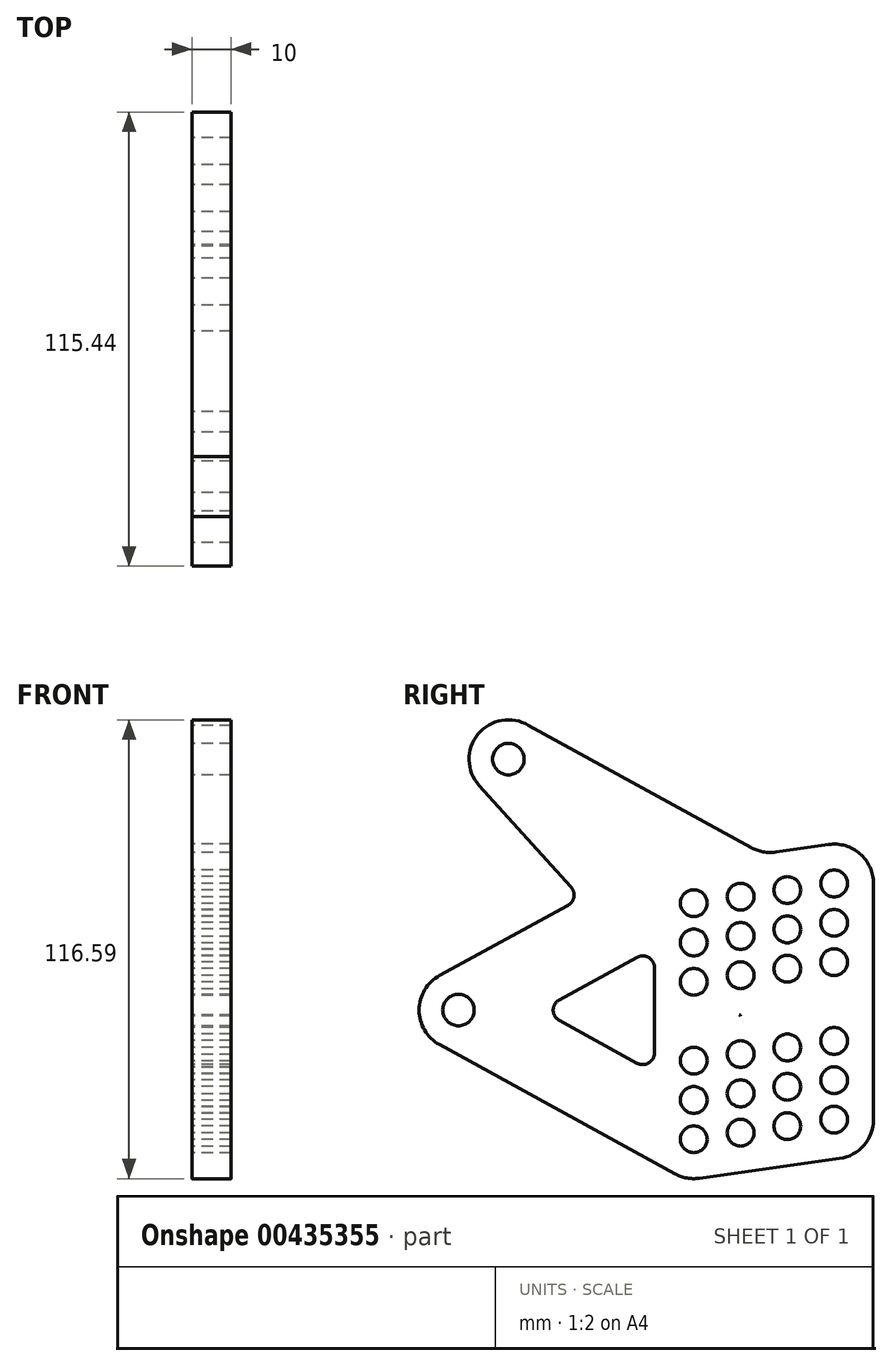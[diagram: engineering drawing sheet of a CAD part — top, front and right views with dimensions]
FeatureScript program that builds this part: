
annotation { "Feature Type Name" : "Feature", "Feature Type Description" : "" }
export const myFeature = defineFeature(function(context is Context, id is Id, definition is map)
    precondition{}
    {
        {
            var Q0;
            Q0=qCreatedBy(makeId("Right.planeOp"),FACE);
            var sketch = newSketch(context, id + "F0", { "sketchPlane" : qUnion([Q0])});
            skCircle(sketch, "E0", {"center": v(-13.5, -7.97) * mm, "radius": 4 * mm});
            skCircle(sketch, "E1", {"center": v(-0.82, 55.78) * mm, "radius": 4 * mm});
            skCircle(sketch, "E2", {"center": v(106.29, -0.8) * mm, "radius": 3.4 * mm});
            skPoint(sketch, "E3.start.orphan", {"position": v(-0.67, 56.85) * mm});
            skPoint(sketch, "E4.start.orphan", {"position": v(-13.3, -6.9) * mm});
            skLineSegment(sketch, "E5.trimOffspring", {"start": v(102.9, -1.01) * mm, "end": v(106.29, -0.8) * mm});
            skLineSegment(sketch, "E6", {"start": v(106.29, -0.8) * mm, "end": v(102.89, -0.8) * mm});
            skCircle(sketch, "E7", {"center": v(46.29, -0.8) * mm, "radius": 3.4 * mm});
            skCircle(sketch, "E8", {"center": v(46.29, -40.8) * mm, "radius": 3.4 * mm});
            skLineSegment(sketch, "E9", {"start": v(70.06, -0.8) * mm, "end": v(70.06, -4.07) * mm});
            skLineSegment(sketch, "E10", {"start": v(79.19, -26.2) * mm, "end": v(78.57, -26.28) * mm});
            skCircle(sketch, "E11", {"center": v(46.29, -30.8) * mm, "radius": 3.4 * mm});
            skCircle(sketch, "E12", {"center": v(46.29, -20.8) * mm, "radius": 3.4 * mm});
            skCircle(sketch, "E13", {"center": v(46.29, 9.2) * mm, "radius": 3.4 * mm});
            skCircle(sketch, "E14", {"center": v(46.29, 19.2) * mm, "radius": 3.4 * mm});
            skCircle(sketch, "E15", {"center": v(58.17, 20.86) * mm, "radius": 3.4 * mm});
            skCircle(sketch, "E16", {"center": v(58.17, 0.86) * mm, "radius": 3.4 * mm});
            skCircle(sketch, "E17", {"center": v(70.06, 12.53) * mm, "radius": 3.4 * mm});
            skCircle(sketch, "E18", {"center": v(58.17, 10.86) * mm, "radius": 3.4 * mm});
            skCircle(sketch, "E19", {"center": v(70.06, 2.53) * mm, "radius": 3.4 * mm});
            skCircle(sketch, "E20", {"center": v(81.94, 4.2) * mm, "radius": 3.4 * mm});
            skCircle(sketch, "E21", {"center": v(81.94, 14.2) * mm, "radius": 3.4 * mm});
            skCircle(sketch, "E22", {"center": v(81.94, 24.2) * mm, "radius": 3.4 * mm});
            skCircle(sketch, "E23", {"center": v(70.06, 22.53) * mm, "radius": 3.4 * mm});
            skCircle(sketch, "E24", {"center": v(58.17, -19.14) * mm, "radius": 3.4 * mm});
            skCircle(sketch, "E25", {"center": v(70.06, -17.47) * mm, "radius": 3.4 * mm});
            skCircle(sketch, "E26", {"center": v(81.94, -15.8) * mm, "radius": 3.4 * mm});
            skCircle(sketch, "E27", {"center": v(58.17, -29.14) * mm, "radius": 3.4 * mm});
            skCircle(sketch, "E28", {"center": v(70.06, -27.47) * mm, "radius": 3.4 * mm});
            skCircle(sketch, "E29", {"center": v(81.94, -25.8) * mm, "radius": 3.4 * mm});
            skCircle(sketch, "E30", {"center": v(81.94, -35.8) * mm, "radius": 3.4 * mm});
            skCircle(sketch, "E31", {"center": v(70.06, -37.47) * mm, "radius": 3.4 * mm});
            skCircle(sketch, "E32", {"center": v(58.17, -39.14) * mm, "radius": 3.4 * mm});
            skPoint(sketch, "E33.end.orphan", {"position": v(85.34, 4.2) * mm});
            skArc(sketch, "E34", {"start": v(83.33, -45.71) * mm, "mid": v(89.49, -42.37) * mm, "end": v(91.94, -35.8) * mm});
            skLineSegment(sketch, "E35", {"start": v(91.94, -35.8) * mm, "end": v(91.94, 24.2) * mm});
            skArc(sketch, "E36", {"start": v(2.5, 65.21) * mm, "mid": v(-9.14, 61.32) * mm, "end": v(-8.24, 49.08) * mm});
            skArc(sketch, "E37", {"start": v(-18.3, 0.8) * mm, "mid": v(-23.5, -7.96) * mm, "end": v(-18.31, -16.74) * mm});
            skLineSegment(sketch, "E38", {"start": v(41.47, -49.57) * mm, "end": v(-18.31, -16.74) * mm});
            skArc(sketch, "E39", {"start": v(41.47, -49.57) * mm, "mid": v(44.48, -50.64) * mm, "end": v(47.68, -50.71) * mm});
            skLineSegment(sketch, "E40", {"start": v(47.68, -50.71) * mm, "end": v(83.33, -45.71) * mm});
            skLineSegment(sketch, "E41", {"start": v(36.29, 19.2) * mm, "end": v(36.29, 19.24) * mm});
            skLineSegment(sketch, "E42", {"start": v(-8.24, 49.08) * mm, "end": v(15.09, 23.26) * mm});
            skLineSegment(sketch, "E43", {"start": v(-18.3, 0.8) * mm, "end": v(14.3, 18.62) * mm});
            skArc(sketch, "E44.filletArc", {"start": v(14.3, 18.62) * mm, "mid": v(15.82, 20.75) * mm, "end": v(15.09, 23.26) * mm});
            skLineSegment(sketch, "E45", {"start": v(36.29, 2.79) * mm, "end": v(36.29, -18.84) * mm});
            skLineSegment(sketch, "E46", {"start": v(12.11, -10.63) * mm, "end": v(31.84, -21.46) * mm});
            skLineSegment(sketch, "E47", {"start": v(12.12, -5.37) * mm, "end": v(31.85, 5.42) * mm});
            skArc(sketch, "E48.filletArc", {"start": v(12.12, -5.37) * mm, "mid": v(10.56, -8) * mm, "end": v(12.11, -10.63) * mm});
            skArc(sketch, "E49.filletArc", {"start": v(36.29, 2.79) * mm, "mid": v(34.82, 5.37) * mm, "end": v(31.85, 5.42) * mm});
            skArc(sketch, "E50.filletArc", {"start": v(31.84, -21.46) * mm, "mid": v(34.82, -21.42) * mm, "end": v(36.29, -18.84) * mm});
            skLineSegment(sketch, "E51.trimOffspring", {"start": v(57.88, -9.18) * mm, "end": v(58.17, -9.5) * mm});
            skLineSegment(sketch, "E52.trimOffspring", {"start": v(58.17, -9.14) * mm, "end": v(58.17, -9.5) * mm});
            skLineSegment(sketch, "E53.trimOffspring", {"start": v(58.17, -9.14) * mm, "end": v(57.88, -9.18) * mm});
            skArc(sketch, "E54.trimOffspring", {"start": v(79.19, -26.2) * mm, "mid": v(78.89, -26.28) * mm, "end": v(78.59, -26.39) * mm});
            skLineSegment(sketch, "E55.trimOffspring", {"start": v(70.73, -0.8) * mm, "end": v(69.39, -0.8) * mm});
            skPoint(sketch, "E56.orphan", {"position": v(-26.68, -7.97) * mm});
            skPoint(sketch, "E57.orphan", {"position": v(-15.63, 55.78) * mm});
            skPoint(sketch, "E58.center.orphan", {"position": v(46.29, 39.2) * mm});
            skPoint(sketch, "E59.center.orphan", {"position": v(58.17, 40.86) * mm});
            skPoint(sketch, "E60.center.orphan", {"position": v(70.06, 42.53) * mm});
            skPoint(sketch, "E61.center.orphan", {"position": v(81.94, 44.2) * mm});
            skArc(sketch, "E62", {"start": v(4.32, 64.36) * mm, "mid": v(-8.54, 62.13) * mm, "end": v(-8.24, 49.08) * mm});
            skPoint(sketch, "E63.center.orphan", {"position": v(58.17, 30.86) * mm});
            skArc(sketch, "E64", {"start": v(91.94, 24.2) * mm, "mid": v(88.5, 31.75) * mm, "end": v(80.52, 34.1) * mm});
            skLineSegment(sketch, "E65", {"start": v(67.1, 32.17) * mm, "end": v(80.52, 34.1) * mm});
            skLineSegment(sketch, "E66", {"start": v(4.32, 64.36) * mm, "end": v(60.86, 33.3) * mm});
            skLineSegment(sketch, "E67", {"start": v(63.08, 32.41) * mm, "end": v(62.85, 32.57) * mm});
            skPoint(sketch, "E68.newPointA", {"position": v(65.31, 30.86) * mm});
            skArc(sketch, "E68.filletArc", {"start": v(60.86, 33.3) * mm, "mid": v(63.89, 32.23) * mm, "end": v(67.1, 32.17) * mm});
            skSolve(sketch);
        }
        {
            var Q0;
            Q0=makeQuery(id+"F0.imprint","IMPRINT",FACE,{"disambiguationData":[TD([[makeQuery(id+"F0.imprint","IMPRINT",EDGE,{"derivedFrom":sQuery(id+"F0.wireOp",EDGE,"E0")}),-1.0]])]});
            extrude(context, id + "F1", {"entities" : qUnion([Q0]), "depth" : 10 * mm, "offsetDistance" : 25 * mm});
        }
    });
